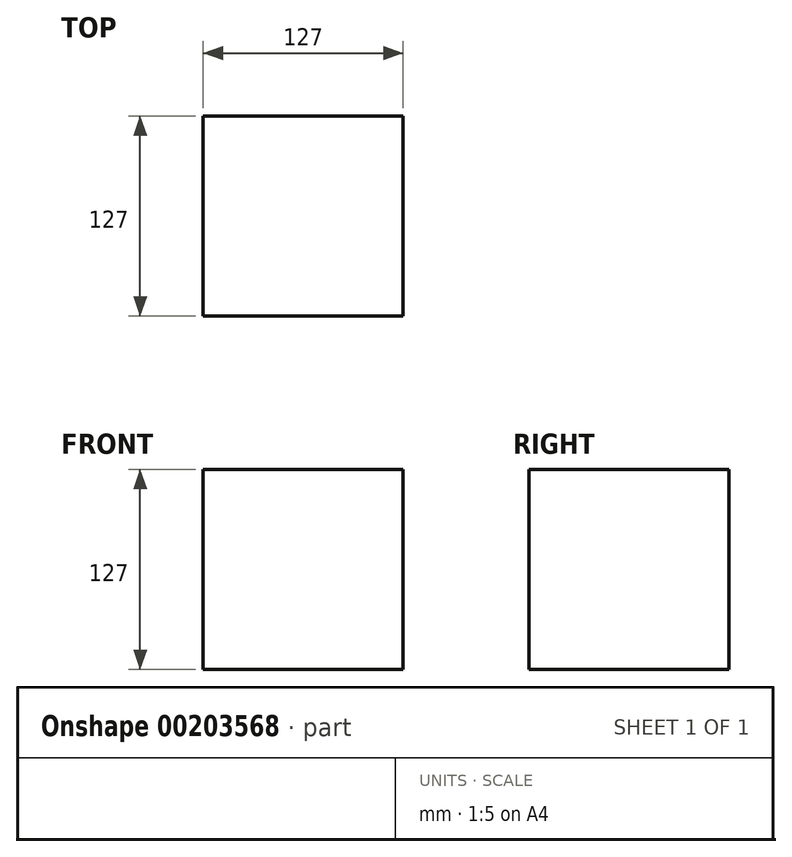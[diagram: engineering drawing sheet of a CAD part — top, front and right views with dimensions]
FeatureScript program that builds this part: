
annotation { "Feature Type Name" : "Feature", "Feature Type Description" : "" }
export const myFeature = defineFeature(function(context is Context, id is Id, definition is map)
    precondition{}
    {
        {
            var Q0;
            Q0=qCreatedBy(makeId("Right.planeOp"),FACE);
            var sketch = newSketch(context, id + "F0", { "sketchPlane" : qUnion([Q0])});
            skLineSegment(sketch, "E0.bottom", {"start": v(0, 127) * mm, "end": v(127, 127) * mm});
            skLineSegment(sketch, "E0.top", {"start": v(0, 0) * mm, "end": v(127, 0) * mm});
            skLineSegment(sketch, "E0.left", {"start": v(0, 127) * mm, "end": v(0, 0) * mm});
            skLineSegment(sketch, "E0.right", {"start": v(127, 127) * mm, "end": v(127, 0) * mm});
            skSolve(sketch);
        }
        {
            var Q0;
            Q0 = qSketchRegion(id + "F0", true);
            extrude(context, id + "F1", {"entities" : qUnion([Q0]), "depth" : 127 * mm});
        }
    });
